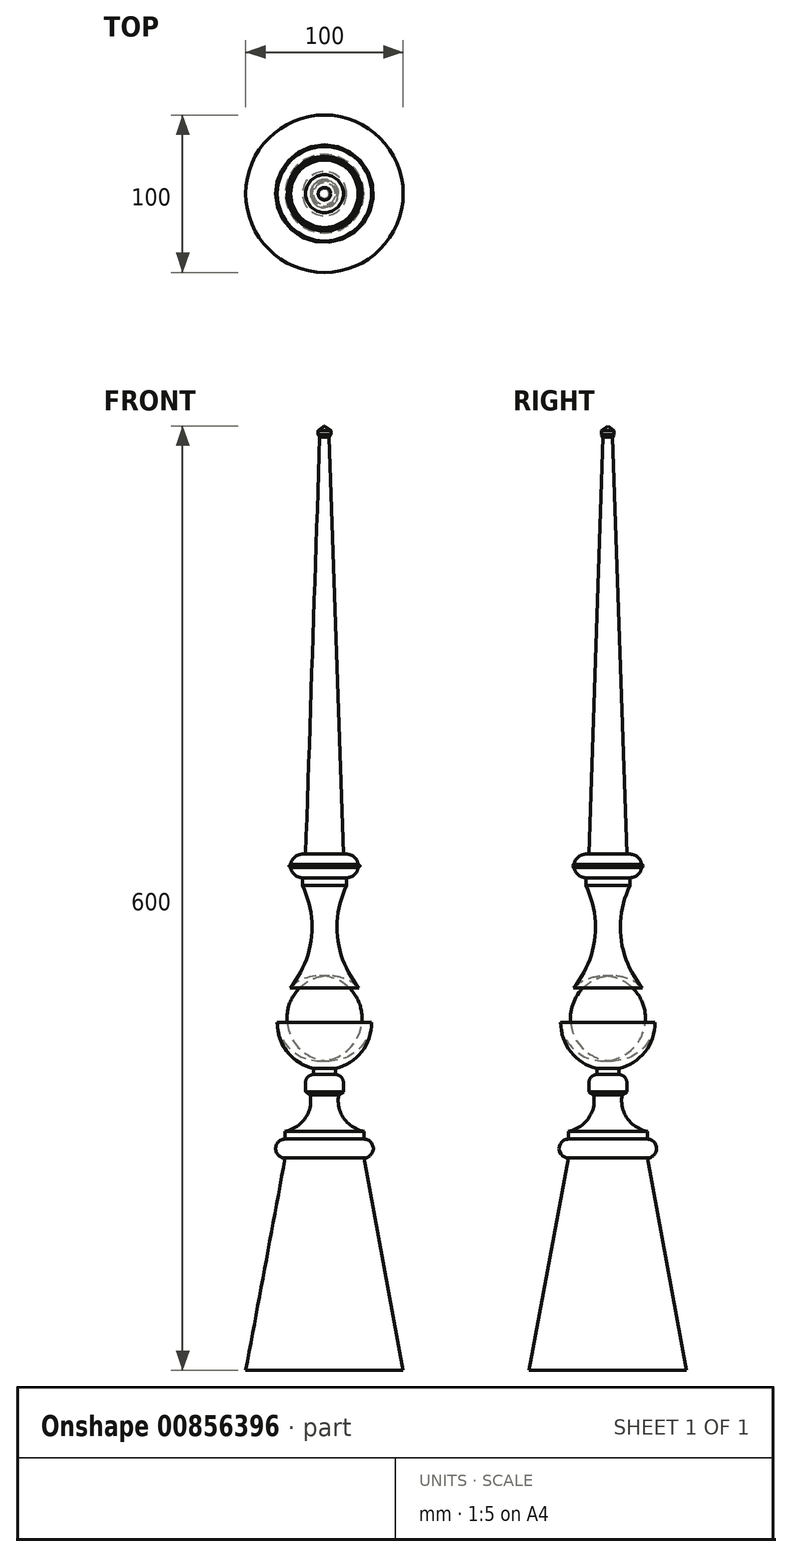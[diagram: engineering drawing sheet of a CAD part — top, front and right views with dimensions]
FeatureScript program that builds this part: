
annotation { "Feature Type Name" : "Feature", "Feature Type Description" : "" }
export const myFeature = defineFeature(function(context is Context, id is Id, definition is map)
    precondition{}
    {
        {
            var Q0;
            Q0=qCreatedBy(makeId("Front.planeOp"),FACE);
            var sketch = newSketch(context, id + "F0", { "sketchPlane" : qUnion([Q0])});
            skLineSegment(sketch, "E0", {"start": v(0, 0) * mm, "end": v(0, 600) * mm});
            skSolve(sketch);
        }
        {
            var Q0;
            Q0=qCreatedBy(makeId("Front.planeOp"),FACE);
            var sketch = newSketch(context, id + "F1", { "sketchPlane" : qUnion([Q0])});
            skPoint(sketch, "E1.0", {"position": v(0, 0) * mm});
            skLineSegment(sketch, "E2", {"start": v(0, 0) * mm, "end": v(50, 0) * mm});
            skLineSegment(sketch, "E3", {"start": v(50, 0) * mm, "end": v(25, 135) * mm});
            skLineSegment(sketch, "E4", {"start": v(25, 135) * mm, "end": v(0, 135) * mm});
            skLineSegment(sketch, "E5", {"start": v(0, 135) * mm, "end": v(0, 0) * mm});
            skLineSegment(sketch, "E6", {"start": v(0, 147) * mm, "end": v(25, 147) * mm});
            skArc(sketch, "E7", {"start": v(25, 135) * mm, "mid": v(31, 141) * mm, "end": v(25, 147) * mm});
            skLineSegment(sketch, "E8", {"start": v(0, 135) * mm, "end": v(0, 147) * mm});
            skLineSegment(sketch, "E9", {"start": v(25, 147) * mm, "end": v(25, 152) * mm});
            skLineSegment(sketch, "E10", {"start": v(0, 175) * mm, "end": v(9, 175) * mm});
            skArc(sketch, "E11", {"start": v(9, 175) * mm, "mid": v(12.3, 160.23) * mm, "end": v(25, 152) * mm});
            skLineSegment(sketch, "E12", {"start": v(0, 188) * mm, "end": v(7, 188) * mm});
            skLineSegment(sketch, "E13", {"start": v(7, 188) * mm, "end": v(7, 191) * mm});
            skLineSegment(sketch, "E14", {"start": v(7, 191) * mm, "end": v(0, 191) * mm, "construction": true});
            skLineSegment(sketch, "E15", {"start": v(9, 175) * mm, "end": v(12, 177) * mm});
            skLineSegment(sketch, "E16", {"start": v(12, 177) * mm, "end": v(12, 183) * mm});
            skArc(sketch, "E17", {"start": v(12, 183) * mm, "mid": v(10.54, 186.54) * mm, "end": v(7, 188) * mm});
            skLineSegment(sketch, "E18", {"start": v(0, 188) * mm, "end": v(0, 147) * mm});
            skLineSegment(sketch, "E19", {"start": v(0, 221) * mm, "end": v(30, 221) * mm});
            skLineSegment(sketch, "E20", {"start": v(0, 221) * mm, "end": v(0, 191) * mm});
            skArc(sketch, "E21", {"start": v(0, 191) * mm, "mid": v(3.52, 191.2) * mm, "end": v(7, 191.83) * mm});
            skLineSegment(sketch, "E22", {"start": v(7, 191.83) * mm, "end": v(7, 191) * mm});
            skArc(sketch, "E23", {"start": v(7, 191.83) * mm, "mid": v(23.56, 202.43) * mm, "end": v(30, 221) * mm});
            skPoint(sketch, "E24", {"position": v(22, 243) * mm});
            skPoint(sketch, "E25", {"position": v(14, 308) * mm});
            skArc(sketch, "E26", {"start": v(30, 221) * mm, "mid": v(28.5, 232.91) * mm, "end": v(22, 243) * mm});
            skArc(sketch, "E27", {"start": v(14, 308) * mm, "mid": v(8.35, 274.31) * mm, "end": v(22, 243) * mm});
            skLineSegment(sketch, "E28", {"start": v(14, 308) * mm, "end": v(0, 308) * mm});
            skLineSegment(sketch, "E29", {"start": v(0, 308) * mm, "end": v(0, 221) * mm});
            skLineSegment(sketch, "E30", {"start": v(0, 191) * mm, "end": v(0, 188) * mm});
            skLineSegment(sketch, "E31", {"start": v(14, 308) * mm, "end": v(14, 313) * mm});
            skLineSegment(sketch, "E32", {"start": v(14, 313) * mm, "end": v(0, 313) * mm});
            skLineSegment(sketch, "E33", {"start": v(0, 328) * mm, "end": v(14, 328) * mm});
            skArc(sketch, "E34", {"start": v(14, 313) * mm, "mid": v(18.94, 314.85) * mm, "end": v(21.43, 319.5) * mm});
            skPoint(sketch, "E35", {"position": v(21.5, 320.5) * mm});
            skPoint(sketch, "E36", {"position": v(21.43, 321.5) * mm});
            skPoint(sketch, "E37", {"position": v(21.43, 319.5) * mm});
            skArc(sketch, "E38", {"start": v(21.43, 319.5) * mm, "mid": v(22.43, 320.5) * mm, "end": v(21.43, 321.5) * mm});
            skLineSegment(sketch, "E39", {"start": v(12, 328) * mm, "end": v(3, 593) * mm});
            skArc(sketch, "E40", {"start": v(21.43, 321.5) * mm, "mid": v(18.94, 326.15) * mm, "end": v(14, 328) * mm});
            skArc(sketch, "E41", {"start": v(21.43, 319.5) * mm, "mid": v(21.5, 320.5) * mm, "end": v(21.43, 321.5) * mm, "construction": true});
            skLineSegment(sketch, "E42", {"start": v(3, 593) * mm, "end": v(4, 594.5) * mm});
            skLineSegment(sketch, "E43", {"start": v(4, 594.5) * mm, "end": v(4, 597) * mm});
            skLineSegment(sketch, "E44", {"start": v(4, 597) * mm, "end": v(0, 600) * mm});
            skLineSegment(sketch, "E45", {"start": v(0, 600) * mm, "end": v(0, 328) * mm});
            skLineSegment(sketch, "E46", {"start": v(0, 328) * mm, "end": v(0, 308) * mm});
            skSolve(sketch);
        }
        {
            var Q0;
            Q0 = qSketchRegion(id + "F1", true);
            var Q1;
            Q1=sQuery(id+"F0.wireOp",EDGE,"E0");
            revolve(context, id + "F2", {"surfaceOperationType" : NewSurfaceOperationType.NEW, "entities" : qUnion([Q0]), "axis" : qUnion([Q1]), "revolveType" : RevolveType.FULL});
        }
    });
